# Revit family: Murfor Compact I-50 Masonry Reinforcement
name_source: partatom
category: Specialty Equipment
revit_build: Autodesk Revit 2018 (Build: 20190510_1515(x64)
units: mm (PartAtom-declared; Revit-internal decimal feet)

## family parameters
Always vertical = Yes
Cut with Voids When Loaded = No
Part Type = Normal
Room Calculation Point = No
Round Connector Dimension = Use Diameter
Shared = No
Work Plane-Based = No

## types (1)
- Murfor Compact I-50
    Application = Murfor Compact I-50, made of Galvanized Steel, is suitable for masonry (clay bricks, concrete blocks) exposed to a dry environment (exposure class MX1, compliant with Eurocode 6?EN845-3)
    Datasheet = https://www.bekaert.com
    Description = Compact masonry reinforcement, steel chords on interwoven fibreglass roving
    Keynote = Suitable for all mortar joints with thickness between 3mm & 12mm
    Longtidinal Cord = 1 mm  [stored 0.00328084 ft]
    Manufacturer = Bekaert
    Material = Murfor Galvanized Steel
    Material Coating Reference EN845-3 = R20
    Pitch (long) - b = 10 mm  [stored 0.0328084 ft]
    Pitch (short) - a = 8 mm  [stored 0.0262467 ft]
    Steel Section Total = 5 mm  [stored 0.0164042 ft]
    Step c = 33 mm  [stored 0.108268 ft]
    Strain Agt = 2.2
    Thickness - e = 2 mm  [stored 0.00656168 ft]
    Type Comments = A mesh consisting of 7 steel chords
    Type Image = Murfor Compact I-50.PNG
    URL = https://www.bekaert.com
    Weight kg/ roll = 1.40kg per roll
    Width - w = 50 mm
    Yield Strength - Mpa = 1770
    Youngs Modulus - Gpa = 180
    Z = 52 mm

note: [stored X ft] marks values corroborated as IEEE doubles in the binary element streams (Revit-internal decimal feet)

## geometry (parser evidence)
native form markers: Blend x4, Sweep x14
no freeform markers — native parametric forms only
